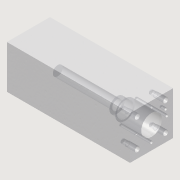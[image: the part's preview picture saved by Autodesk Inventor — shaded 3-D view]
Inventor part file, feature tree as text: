
AUTODESK INVENTOR PART (.ipt)
format: ipt  version: 2014 (Build 180170000, 170)  size: 344,576 bytes
history: native  units: mm
features: other x48, extrude x21, sketch x21
ambient origin geometry x8: Origin, YZ Plane, XZ Plane, XY Plane, X Axis, Y Axis, Z Axis, Center Point
bodies: 实体1 (feature_tree)
feature tree (90):
  extrude  "拉伸1"  Depth=33.7mm
  other  "UCS1"
  other  "UCS2"
  other  "UCS3"
  other  "UCS4"
  other  "UCS5"
  other  "UCS6"
  extrude  "拉伸23"  Depth=35.0mm
  extrude  "拉伸24"  Depth=65.0mm
  extrude  "拉伸25"  Depth=10.0mm
  extrude  "拉伸26"  Depth=43.0mm
  extrude  "拉伸28"  Depth=13.0mm
  extrude  "拉伸29"  Depth=16.0mm
  extrude  "拉伸30"  Depth=152.4mm
  extrude  "拉伸31"  Depth=23.0mm
  extrude  "拉伸32"  Depth=23.0mm
  extrude  "拉伸33"  Depth=23.0mm
  extrude  "拉伸34"  Depth=23.0mm
  extrude  "拉伸35"  Depth=24.0mm TaperAngle=0.0deg
  extrude  "拉伸36"  Depth=24.0mm
  extrude  "拉伸37"  Depth=200.0mm
  extrude  "拉伸38"  Depth=8.0mm
  extrude  "拉伸39"  Depth=16.0mm TaperAngle=0.0deg
  extrude  "拉伸40"  Depth=4.0mm
  extrude  "拉伸41"  Depth=4.0mm
  extrude  "拉伸42"  TaperAngle=0.0deg  [1 undecoded]
  extrude  "拉伸43"  TaperAngle=0.0deg  [1 undecoded]
  sketch  "草图1"  dims[d0=70.0mm d1=0.0mm]
  sketch  "草图27"  dims[d2=0.0mm d3=0.0mm d4=0.0mm d5=0.0mm d6=0.0mm d7=0.0mm]
  sketch  "草图28"  dims[d8=0.0mm d9=0.0mm d10=0.0mm d11=0.0mm d12=0.0mm d13=0.0mm]
  sketch  "草图29"  dims[d14=0.0mm d15=0.0mm d16=0.0mm d17=0.0mm d18=0.0mm d19=0.0mm]
  sketch  "草图31"  dims[d20=0.0mm d21=0.0mm d22=0.0mm d23=0.0mm d24=0.0mm d25=0.0mm]
  sketch  "草图32"  dims[d26=0.0mm d27=0.0mm d28=0.0mm d29=0.0mm d30=0.0mm d31=0.0mm]
  sketch  "草图33"  dims[d32=0.0mm d33=0.0mm d34=0.0mm d35=0.0mm d36=0.0mm d37=0.0mm d110=33.7mm]
  sketch  "草图34"  dims[d111=36.0mm d112=35.0mm]
  sketch  "草图35"  dims[d113=65.0mm d114=65.0mm]
  sketch  "草图36"  dims[d115=10.0mm d116=-2.617994mm d117=32.0mm]
  sketch  "草图37"  dims[d118=43.0mm d119=0.0mm d120=26.07mm]
  sketch  "草图38"  dims[d121=13.0mm d122=-2.617994mm d124=25.0mm]
  sketch  "草图39"  dims[d125=56.0mm d126=0.0mm d127=16.0mm]
  sketch  "草图40"  dims[d130=152.4mm d131=0.0mm d132=152.4mm d133=-10.297443mm]
  sketch  "草图41"  dims[d134=6.75mm d135=23.0mm]
  sketch  "草图42"  dims[d136=23.0mm d137=23.0mm]
  sketch  "草图43"  dims[d138=23.0mm d139=23.0mm]
  sketch  "草图44"  dims[d140=23.0mm d141=23.0mm]
  sketch  "草图45"  dims[d142=23.0mm d143=24.0mm d144=0.0mm]
  sketch  "草图46"  dims[d145=24.0mm d146=-10.297443mm d147=24.0mm d148=-10.297443mm]
  sketch  "草图47"  dims[d149=24.0mm d150=-10.297443mm d151=24.0mm d152=-10.297443mm d153=8.0mm d154=16.0mm d155=0.0mm d156=4.0mm d157=4.0mm d160=0.0mm d161=0.0mm d162=25.0mm d163=25.000195mm d164=25.4mm d165=0.0mm d166=25.4mm d167=-10.297443mm d168=25.4mm d169=-10.297443mm d170=4.0mm d171=4.0mm d172=25.0mm d173=0.0mm d174=25.0mm d175=0.0mm d176=25.4mm d177=0.0mm d178=25.4mm d179=-10.297443mm d180=25.4mm d181=-10.297443mm d182=4.0mm d183=23.0mm d184=10.5mm d185=8.0mm d186=0.0mm d187=8.0mm d188=-10.297443mm d294=70.0mm d295=200.0mm]
  other  "UCS1: YZ 平面"
  other  "UCS1: XZ 平面"
  other  "UCS1: XY 平面"
  other  "UCS1: X 轴"
  other  "UCS1: Y 轴"
  other  "UCS1: Z 轴"
  other  "UCS1: 原点"
  other  "UCS2: YZ 平面"
  other  "UCS2: XZ 平面"
  other  "UCS2: XY 平面"
  other  "UCS2: X 轴"
  other  "UCS2: Y 轴"
  other  "UCS2: Z 轴"
  other  "UCS2: 原点"
  other  "UCS3: YZ 平面"
  other  "UCS3: XZ 平面"
  other  "UCS3: XY 平面"
  other  "UCS3: X 轴"
  other  "UCS3: Y 轴"
  other  "UCS3: Z 轴"
  other  "UCS3: 原点"
  other  "UCS4: YZ 平面"
  other  "UCS4: XZ 平面"
  other  "UCS4: XY 平面"
  other  "UCS4: X 轴"
  other  "UCS4: Y 轴"
  other  "UCS4: Z 轴"
  other  "UCS4: 原点"
  other  "UCS5: YZ 平面"
  other  "UCS5: XZ 平面"
  other  "UCS5: XY 平面"
  other  "UCS5: X 轴"
  other  "UCS5: Y 轴"
  other  "UCS5: Z 轴"
  other  "UCS5: 原点"
  other  "UCS6: YZ 平面"
  other  "UCS6: XZ 平面"
  other  "UCS6: XY 平面"
  other  "UCS6: X 轴"
  other  "UCS6: Y 轴"
  other  "UCS6: Z 轴"
  other  "UCS6: 原点"
note: 2 required parameter values undecoded (feature->parameter linkage not recoverable at this tier; creation-order binding heuristic only, values carry confidence <= 0.55)
